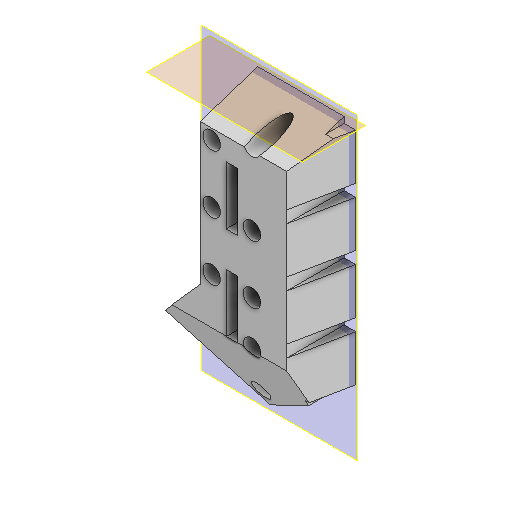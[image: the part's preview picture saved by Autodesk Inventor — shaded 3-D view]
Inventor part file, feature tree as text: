
AUTODESK INVENTOR PART (.ipt)
format: ipt  version: 2025.1 (Build 291241020, 241B)  size: 365,056 bytes
history: native  units: in
note: dims shown in document units (in); Inventor stores cm internally (conversion verified against a paired STEP export)
features: reference x48, other x12, extrude x9, sketch x9, plane x2, chamfer x1, projected_geometry x1
ambient origin geometry x8: Origin, YZ Plane, XZ Plane, XY Plane, X Axis, Y Axis, Z Axis, Center Point
bodies: Solid1 (feature_tree)
feature tree (82):
  extrude  "Extrusion1"  Depth=0.25in TaperAngle=0.0deg
  extrude  "Extrusion2"  Depth=0.14in
  extrude  "Extrusion3"  Depth=0.14in
  plane  "Work Plane1"
  extrude  "Extrusion4"  Depth=0.14in
  extrude  "Extrusion5"  Depth=0.25in TaperAngle=0.0deg
  extrude  "Extrusion6"  Depth=0.3in
  plane  "Work Plane2"
  extrude  "Extrusion7"  Depth=0.3in
  extrude  "Extrusion9"  Depth=0.25in TaperAngle=0.0deg
  extrude  "Extrusion14"  Depth=0.1in
  chamfer  "Chamfer1"  Distance=0.25in
  sketch  "Sketch1"  dims[d0=0.25in d1=0.0in d2=0.25in d3=0.0in]
  reference  "Reference1"
  reference  "Reference2"
  reference  "Reference3"
  reference  "Reference4"
  reference  "Reference5"
  reference  "Reference6"
  reference  "Reference7"
  reference  "Reference8"
  reference  "Reference9"
  reference  "Reference10"
  reference  "Reference11"
  reference  "Reference12"
  reference  "Reference13"
  reference  "Reference14"
  reference  "Reference15"
  reference  "Reference16"
  reference  "Reference17"
  reference  "Reference18"
  reference  "Reference19"
  reference  "Reference20"
  reference  "Reference21"
  reference  "Reference22"
  reference  "Reference23"
  reference  "Reference24"
  reference  "Reference25"
  reference  "Reference26"
  reference  "Reference27"
  sketch  "Sketch2"  dims[d4=0.7in d5=0.14in d7=0.14in]
  reference  "Reference28"
  reference  "Reference29"
  reference  "Reference30"
  reference  "Reference31"
  reference  "Reference32"
  reference  "Reference33"
  reference  "Reference34"
  reference  "Reference35"
  reference  "Reference36"
  reference  "Reference37"
  reference  "Reference38"
  reference  "Reference39"
  reference  "Reference40"
  reference  "Reference41"
  reference  "Reference42"
  reference  "Reference43"
  sketch  "Sketch3"  dims[d8=0.14in d9=0.14in]
  reference  "Reference44"
  reference  "Reference45"
  reference  "Reference46"
  sketch  "Sketch5"  dims[d10=0.14in d12=0.14in]
  sketch  "Sketch6"  dims[d13=0.35in d14=0.25in d15=0.0in]
  sketch  "Sketch7"  dims[d16=-0.1in d17=0.3in]
  projected_geometry  "Projected Loop1"
  sketch  "Sketch8"  dims[d19=0.3in d20=0.3in]
  sketch  "Sketch10"  dims[d22=0.3in d25=0.25in d26=0.0in]
  reference  "Reference48"
  sketch  "Sketch15"  dims[d27=0.14in d28=0.7in d29=0.25in d30=0.3in d31=0.14in d32=0.25in d33=0.3in d34=0.14in d35=0.3in d36=0.3in d37=0.75in d38=0.0in d40=4.25in d41=0.0in d42=0.25in d43=1.4in d44=0.325in d45=6.3125in d46=0.0in d52=0.6in d53=0.0in d75=2.625in d76=0.0in d77=0.1in d78=0.125in d79=45.0deg d88=0.5in d89=0.0344in d90=0.5in d91=0.0344in]
  reference  "Reference49"
  parser-record x1  (decoder bookkeeping rows leaked as tree rows — omitted from the tree; the rows remain in map.json)
  other  "Hand Assem.iam"
  other  "Thumb Base2:1"
  other  "PALM 3:1"
  other  "PALM 2:1"
  other  "PALM 1:1"
  other  "KNUCKLE 1:1"
  other  "KNUCKLE 2:1"
  other  "KNUCKLE 3:1"
  other  "PALM 4:1"
  other  "KNUCKLE 4:1"
  other  "Palm:1"
note: 1 file-system path scrubbed to <path> (originals preserved in map.json)
